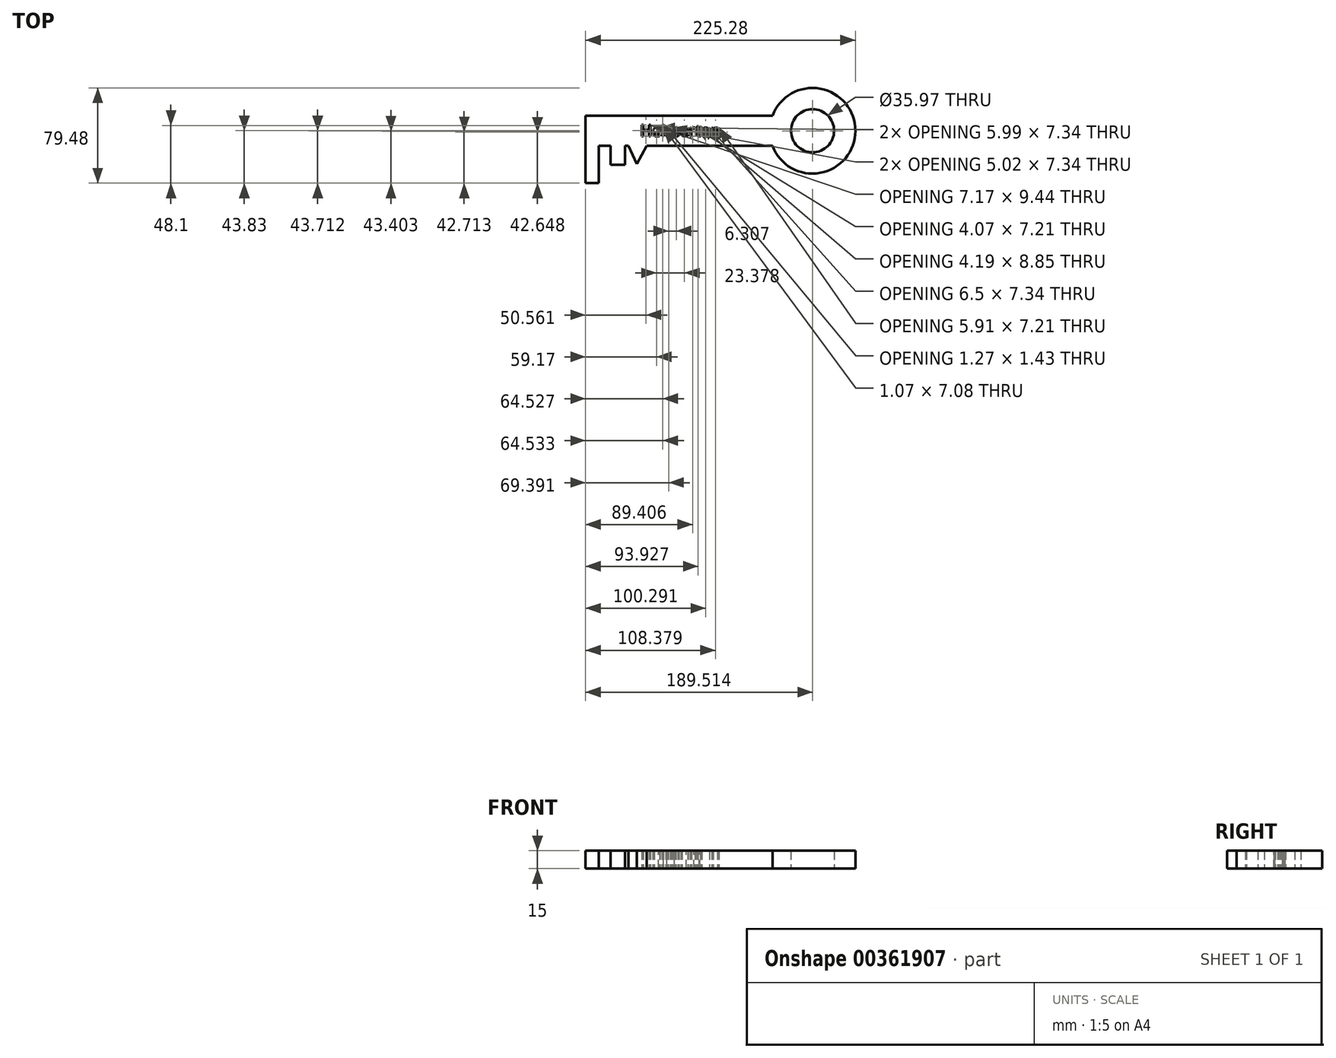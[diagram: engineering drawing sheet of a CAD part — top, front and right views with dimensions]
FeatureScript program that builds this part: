
annotation { "Feature Type Name" : "Feature", "Feature Type Description" : "" }
export const myFeature = defineFeature(function(context is Context, id is Id, definition is map)
    precondition{}
    {
        {
            var Q0;
            Q0=qCreatedBy(makeId("Top.planeOp"),FACE);
            var sketch = newSketch(context, id + "F0", { "sketchPlane" : qUnion([Q0])});
            skLineSegment(sketch, "E0.bottom", {"start": v(-108.18, 25.3) * mm, "end": v(47.88, 25.3) * mm});
            skLineSegment(sketch, "E0.top", {"start": v(-108.18, 0) * mm, "end": v(47.88, 0) * mm});
            skLineSegment(sketch, "E0.left", {"start": v(-108.18, 25.3) * mm, "end": v(-108.18, 0) * mm});
            skLineSegment(sketch, "E1.bottom", {"start": v(-108.18, 0) * mm, "end": v(-97.27, 0) * mm});
            skLineSegment(sketch, "E1.top", {"start": v(-108.18, -31.06) * mm, "end": v(-97.27, -31.06) * mm});
            skLineSegment(sketch, "E1.left", {"start": v(-108.18, 0) * mm, "end": v(-108.18, -31.06) * mm});
            skLineSegment(sketch, "E1.right", {"start": v(-97.27, 0) * mm, "end": v(-97.27, -31.06) * mm});
            skLineSegment(sketch, "E2.bottom", {"start": v(-87.27, 0) * mm, "end": v(-75.3, 0) * mm});
            skLineSegment(sketch, "E2.top", {"start": v(-87.27, -15.9) * mm, "end": v(-75.3, -15.9) * mm});
            skLineSegment(sketch, "E2.left", {"start": v(-87.27, 0) * mm, "end": v(-87.27, -15.9) * mm});
            skLineSegment(sketch, "E2.right", {"start": v(-75.3, 0) * mm, "end": v(-75.3, -15.9) * mm});
            skLineSegment(sketch, "E3", {"start": v(-72.27, 0) * mm, "end": v(-65.3, -15) * mm});
            skLineSegment(sketch, "E4", {"start": v(-65.3, -15) * mm, "end": v(-57.12, 0) * mm});
            skArc(sketch, "E5", {"start": v(47.88, 0) * mm, "mid": v(117.1, 12.65) * mm, "end": v(47.88, 25.3) * mm});
            skCircle(sketch, "E6", {"center": v(81.33, 12.65) * mm, "radius": 17.98 * mm});
            skText(sketch, "E7", { "text": "Heisserton", "fontName": "OpenSans-Regular.ttf"});
            const initialGuessF0  = {"E7": [-0.0625, 0.00805, 1, 0, 0.00952]};
            skSetInitialGuess(sketch, initialGuessF0);
            skSolve(sketch);
        }
        {
            var Q0;
            Q0 = qSketchRegion(id + "F0", true);
            extrude(context, id + "F1", {"entities" : qUnion([Q0]), "depth" : 15 * mm});
        }
    });
